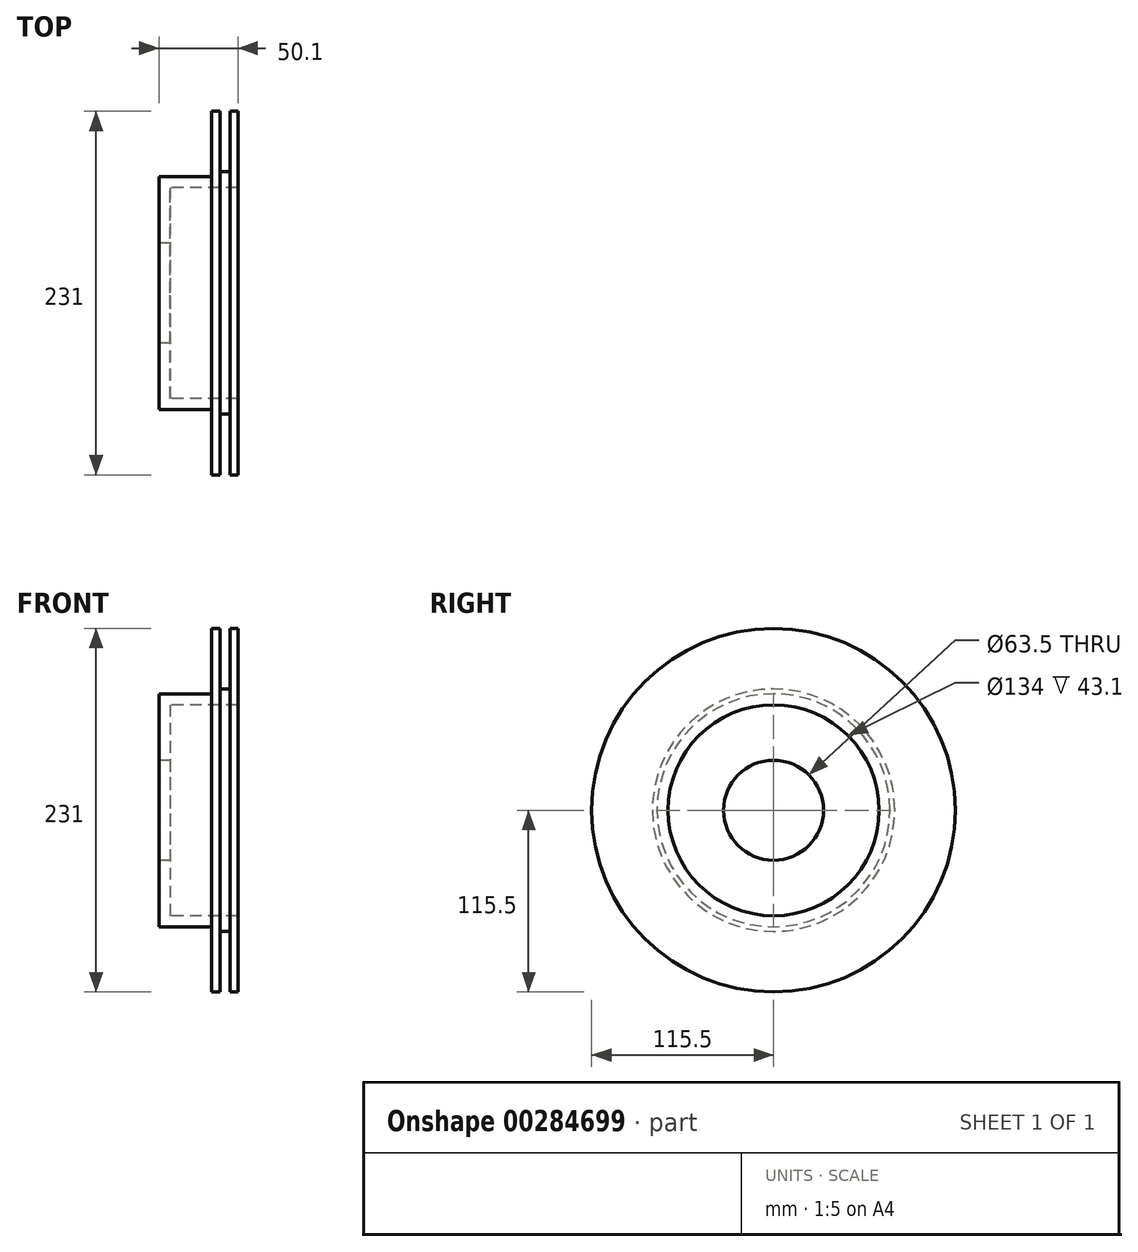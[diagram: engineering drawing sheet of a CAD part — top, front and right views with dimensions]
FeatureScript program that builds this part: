
annotation { "Feature Type Name" : "Feature", "Feature Type Description" : "" }
export const myFeature = defineFeature(function(context is Context, id is Id, definition is map)
    precondition{}
    {
        {
            var Q0;
            Q0=qCreatedBy(makeId("Front.planeOp"),FACE);
            var sketch = newSketch(context, id + "F0", { "sketchPlane" : qUnion([Q0])});
            skLineSegment(sketch, "E0", {"start": v(0, 0) * mm, "end": v(0, 74) * mm});
            skLineSegment(sketch, "E1", {"start": v(0, 0) * mm, "end": v(33.3, 0) * mm});
            skLineSegment(sketch, "E2", {"start": v(33.3, 0) * mm, "end": v(33.3, 74) * mm});
            skLineSegment(sketch, "E3", {"start": v(33.3, 74) * mm, "end": v(0, 74) * mm});
            skLineSegment(sketch, "E4", {"start": v(33.3, 74) * mm, "end": v(33.3, 115.5) * mm});
            skLineSegment(sketch, "E5", {"start": v(33.3, 74) * mm, "end": v(33.3, 67) * mm});
            skLineSegment(sketch, "E6", {"start": v(33.3, 67) * mm, "end": v(7, 67) * mm});
            skLineSegment(sketch, "E7", {"start": v(7, 67) * mm, "end": v(7, 0) * mm});
            skLineSegment(sketch, "E8", {"start": v(33.3, 115.5) * mm, "end": v(38.8, 115.5) * mm});
            skLineSegment(sketch, "E9", {"start": v(38.8, 115.5) * mm, "end": v(38.8, 67) * mm});
            skLineSegment(sketch, "E10", {"start": v(38.8, 67) * mm, "end": v(33.3, 67) * mm});
            skPoint(sketch, "E11", {"position": v(38.8, 77) * mm});
            skPoint(sketch, "E12", {"position": v(50.1, 67) * mm});
            skLineSegment(sketch, "E13", {"start": v(50.1, 67) * mm, "end": v(50.1, 115.5) * mm});
            skLineSegment(sketch, "E14", {"start": v(50.1, 115.5) * mm, "end": v(45.1, 115.5) * mm});
            skLineSegment(sketch, "E15", {"start": v(45.1, 115.5) * mm, "end": v(45.1, 67) * mm});
            skLineSegment(sketch, "E16", {"start": v(45.1, 67) * mm, "end": v(38.8, 67) * mm});
            skLineSegment(sketch, "E17", {"start": v(38.8, 77) * mm, "end": v(45.1, 77) * mm});
            skLineSegment(sketch, "E18", {"start": v(45.1, 67) * mm, "end": v(50.1, 67) * mm});
            skPoint(sketch, "E19", {"position": v(0, 31.75) * mm});
            skPoint(sketch, "E20", {"position": v(0, 0) * mm});
            skLineSegment(sketch, "E21", {"start": v(0, 31.75) * mm, "end": v(7, 31.75) * mm});
            skSolve(sketch);
        }
        {
            var Q0;
            {var subQ1=sQuery(id+"F0.wireOp",EDGE,"E3");Q0=makeQuery(id+"F0.imprint","IMPRINT",FACE,{"disambiguationData":[TD([[makeQuery(id+"F0.imprint","IMPRINT",EDGE,{"derivedFrom":subQ1}),1.0]])]});}
            var Q1;
            Q1=makeQuery(id+"F0.imprint","IMPRINT",FACE,{"disambiguationData":[TD([[makeQuery(id+"F0.imprint","IMPRINT",EDGE,{"derivedFrom":sQuery(id+"F0.wireOp",EDGE,"E4")}),-1.0]])]});
            var Q2;
            {var subQ0=sQuery(id+"F0.wireOp",EDGE,"E16");Q2=makeQuery(id+"F0.imprint","IMPRINT",FACE,{"disambiguationData":[TD([[makeQuery(id+"F0.imprint","IMPRINT",EDGE,{"derivedFrom":subQ0}),-1.0]])]});}
            var Q3;
            Q3=makeQuery(id+"F0.imprint","IMPRINT",FACE,{"disambiguationData":[TD([[makeQuery(id+"F0.imprint","IMPRINT",EDGE,{"derivedFrom":sQuery(id+"F0.wireOp",EDGE,"E13")}),1.0]])]});
            var Q4;
            Q4=sQuery(id+"F0.wireOp",EDGE,"E1");
            revolve(context, id + "F1", {"entities" : qUnion([Q0, Q1, Q2, Q3]), "axis" : qUnion([Q4]), "revolveType" : RevolveType.FULL});
        }
    });
